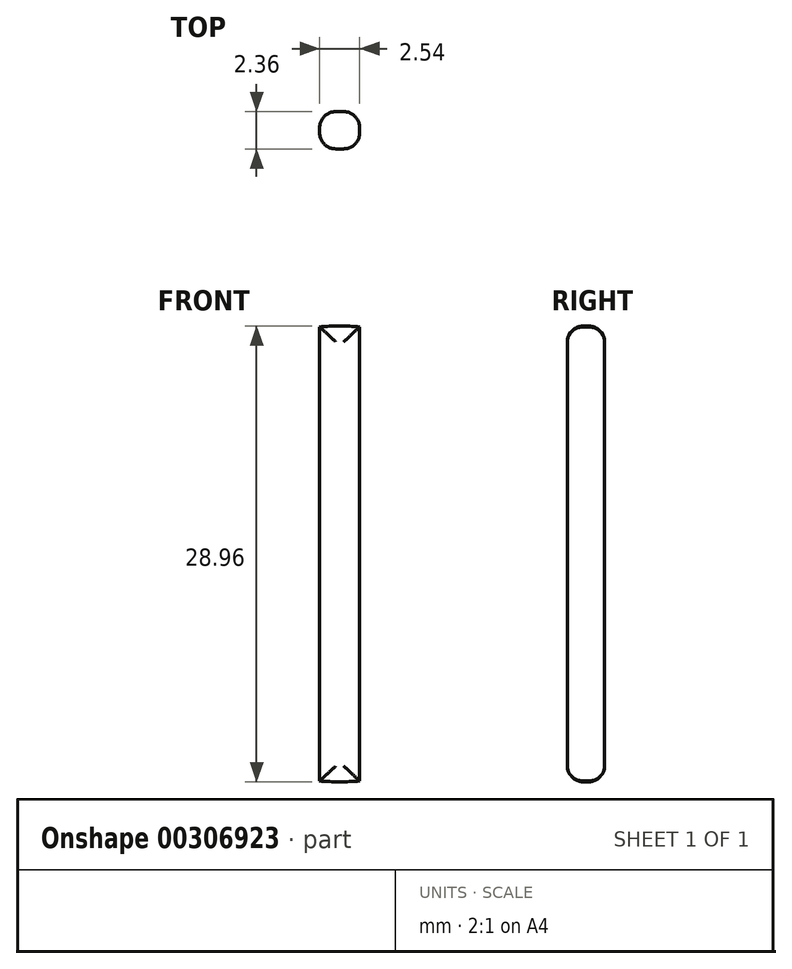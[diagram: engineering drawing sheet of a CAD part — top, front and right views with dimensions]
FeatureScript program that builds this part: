
annotation { "Feature Type Name" : "Feature", "Feature Type Description" : "" }
export const myFeature = defineFeature(function(context is Context, id is Id, definition is map)
    precondition{}
    {
        {
            var Q0;
            Q0=qCreatedBy(makeId("Front.planeOp"),FACE);
            var sketch = newSketch(context, id + "F0", { "sketchPlane" : qUnion([Q0])});
            skCircle(sketch, "E0", {"center": v(0, 0) * mm, "radius": 14.48 * mm});
            skLineSegment(sketch, "E1.bottom", {"start": v(-1.27, -19.18) * mm, "end": v(1.27, -19.18) * mm});
            skLineSegment(sketch, "E1.top", {"start": v(-1.27, 19.18) * mm, "end": v(1.27, 19.18) * mm});
            skLineSegment(sketch, "E1.left", {"start": v(-1.27, -19.18) * mm, "end": v(-1.27, 19.18) * mm});
            skLineSegment(sketch, "E1.right", {"start": v(1.27, -19.18) * mm, "end": v(1.27, 19.18) * mm});
            skSolve(sketch);
        }
        {
            var Q0;
            {var subQ0=sQuery(id+"F0.wireOp",EDGE,"E1.left");var subQ1=sQuery(id+"F0.wireOp",EDGE,"E0");var subQ2=makeQuery(id+"F0.imprint","INTERSECT",VERTEX,{"disambiguationData":[OD(0.0)],"derivedFrom":[subQ1,subQ0]});Q0=makeQuery(id+"F0.imprint","IMPRINT",FACE,{"disambiguationData":[TD([[makeQuery(id+"F0.imprint","IMPRINT",EDGE,{"disambiguationData":[TD([[subQ2,-1.0]])],"derivedFrom":subQ1}),1.0]])]});}
            extrude(context, id + "F1", {"entities" : qUnion([Q0]), "oppositeDirection" : true, "depth" : 2.36 * mm});
        }
        {
            var Q0;
            Q0=makeQuery(id+"F1.opExtrude","CAP_FACE",FACE,{"disambiguationData":[OSD([sQuery(id+"F0.wireOp",EDGE,"E0"),sQuery(id+"F0.wireOp",EDGE,"E1.left")])],"isStart":true});
            var Q1;
            Q1=makeQuery(id+"F1.opExtrude","CAP_FACE",FACE,{"disambiguationData":[OSD([sQuery(id+"F0.wireOp",EDGE,"E0"),sQuery(id+"F0.wireOp",EDGE,"E1.left")])],"isStart":false});
            fillet(context, id + "F2", {"entities" : qUnion([Q0, Q1]), "radius" : 1.02 * mm, "tangentPropagation" : true, "allowEdgeOverflow" : false});
        }
        {
            var Q0;
            Q0=qCreatedBy(makeId("Top.planeOp"),FACE);
            cPlane(context, id + "F3", {"entities" : qUnion([Q0]), "cplaneType" : CPlaneType.OFFSET, "offset" : 17.78 * mm, "oppositeDirection" : true, "width" : 152.4 * mm, "height" : 152.4 * mm});
        }
        {
            var Q0;
            Q0=qCreatedBy(id+"F3.planeOp",FACE);
            var sketch = newSketch(context, id + "F4", { "sketchPlane" : qUnion([Q0])});
            skCircle(sketch, "E2", {"center": v(-2.35, 1.2) * mm, "radius": 1.15 * mm});
            skSolve(sketch);
        }
    });
